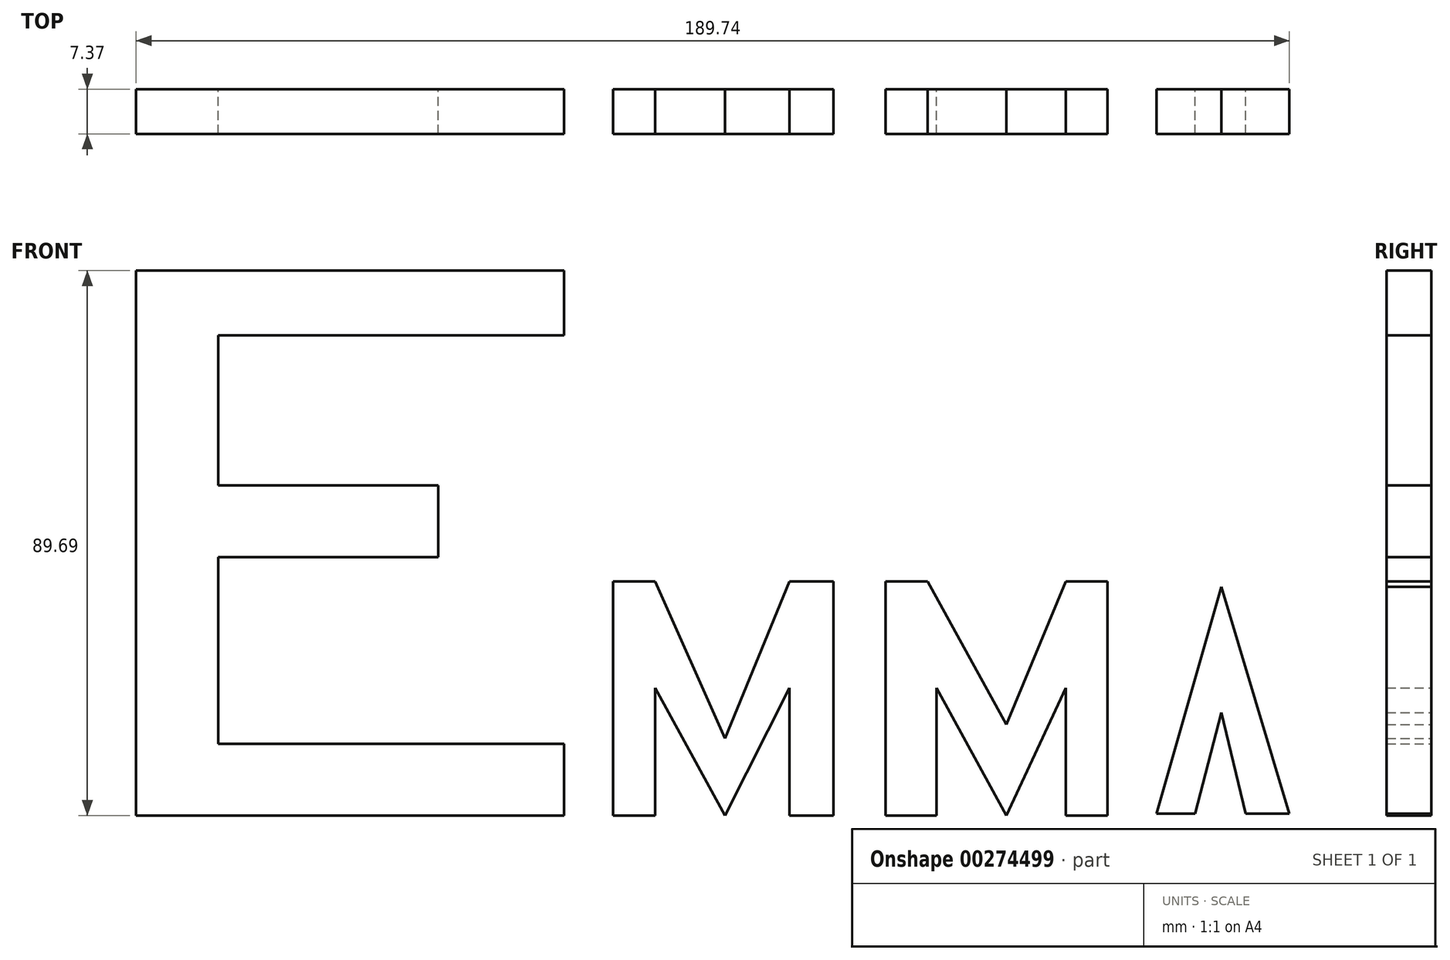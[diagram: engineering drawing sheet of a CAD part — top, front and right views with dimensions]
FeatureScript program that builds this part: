
annotation { "Feature Type Name" : "Feature", "Feature Type Description" : "" }
export const myFeature = defineFeature(function(context is Context, id is Id, definition is map)
    precondition{}
    {
        {
            var Q0;
            Q0=qCreatedBy(makeId("Front.planeOp"),FACE);
            var sketch = newSketch(context, id + "F0", { "sketchPlane" : qUnion([Q0])});
            skLineSegment(sketch, "E0", {"start": v(-135.03, 41.6) * mm, "end": v(-135.03, -48.1) * mm});
            skLineSegment(sketch, "E1", {"start": v(-135.03, -48.1) * mm, "end": v(-64.6, -48.1) * mm});
            skLineSegment(sketch, "E2", {"start": v(-64.6, -48.1) * mm, "end": v(-64.6, -36.32) * mm});
            skLineSegment(sketch, "E3", {"start": v(-64.6, -36.32) * mm, "end": v(-121.52, -36.32) * mm});
            skLineSegment(sketch, "E4", {"start": v(-121.52, -36.32) * mm, "end": v(-121.52, -5.56) * mm});
            skLineSegment(sketch, "E5", {"start": v(-121.52, -5.56) * mm, "end": v(-85.3, -5.56) * mm});
            skLineSegment(sketch, "E6", {"start": v(-85.3, -5.56) * mm, "end": v(-85.3, 6.23) * mm});
            skLineSegment(sketch, "E7", {"start": v(-85.3, 6.23) * mm, "end": v(-121.52, 6.23) * mm});
            skLineSegment(sketch, "E8", {"start": v(-121.52, 6.23) * mm, "end": v(-121.52, 30.95) * mm});
            skLineSegment(sketch, "E9", {"start": v(-121.52, 30.95) * mm, "end": v(-64.6, 30.95) * mm});
            skLineSegment(sketch, "E10", {"start": v(-64.6, 30.95) * mm, "end": v(-64.6, 41.6) * mm});
            skLineSegment(sketch, "E11", {"start": v(-64.6, 41.6) * mm, "end": v(-135.03, 41.6) * mm});
            skLineSegment(sketch, "E12", {"start": v(-56.55, -9.58) * mm, "end": v(-56.55, -48.1) * mm});
            skLineSegment(sketch, "E13", {"start": v(-56.55, -48.1) * mm, "end": v(-49.65, -48.1) * mm});
            skLineSegment(sketch, "E14", {"start": v(-49.65, -48.1) * mm, "end": v(-49.65, -27.12) * mm});
            skLineSegment(sketch, "E15", {"start": v(-49.65, -27.12) * mm, "end": v(-38.15, -48.1) * mm});
            skLineSegment(sketch, "E16", {"start": v(-38.15, -48.1) * mm, "end": v(-27.51, -27.12) * mm});
            skLineSegment(sketch, "E17", {"start": v(-27.51, -27.12) * mm, "end": v(-27.51, -48.1) * mm});
            skLineSegment(sketch, "E18", {"start": v(-27.51, -48.1) * mm, "end": v(-20.33, -48.1) * mm});
            skLineSegment(sketch, "E19", {"start": v(-20.33, -48.1) * mm, "end": v(-20.33, -9.58) * mm});
            skLineSegment(sketch, "E20", {"start": v(-20.33, -9.58) * mm, "end": v(-27.51, -9.58) * mm});
            skLineSegment(sketch, "E21", {"start": v(-27.51, -9.58) * mm, "end": v(-38.15, -35.45) * mm});
            skLineSegment(sketch, "E22", {"start": v(-38.15, -35.45) * mm, "end": v(-49.65, -9.58) * mm});
            skLineSegment(sketch, "E23", {"start": v(-49.65, -9.58) * mm, "end": v(-56.55, -9.58) * mm});
            skLineSegment(sketch, "E24", {"start": v(-11.7, -9.58) * mm, "end": v(-11.7, -48.1) * mm});
            skLineSegment(sketch, "E25", {"start": v(-11.7, -48.1) * mm, "end": v(-3.37, -48.1) * mm});
            skLineSegment(sketch, "E26", {"start": v(-3.37, -48.1) * mm, "end": v(-3.37, -27.12) * mm});
            skLineSegment(sketch, "E27", {"start": v(-3.37, -27.12) * mm, "end": v(8.13, -48.1) * mm});
            skLineSegment(sketch, "E28", {"start": v(8.13, -48.1) * mm, "end": v(17.9, -27.12) * mm});
            skLineSegment(sketch, "E29", {"start": v(17.9, -27.12) * mm, "end": v(17.9, -48.1) * mm});
            skLineSegment(sketch, "E30", {"start": v(17.9, -48.1) * mm, "end": v(24.8, -48.1) * mm});
            skLineSegment(sketch, "E31", {"start": v(24.8, -48.1) * mm, "end": v(24.8, -9.58) * mm});
            skLineSegment(sketch, "E32", {"start": v(24.8, -9.58) * mm, "end": v(17.9, -9.58) * mm});
            skLineSegment(sketch, "E33", {"start": v(17.9, -9.58) * mm, "end": v(8.13, -33.15) * mm});
            skLineSegment(sketch, "E34", {"start": v(8.13, -33.15) * mm, "end": v(-4.78, -9.58) * mm});
            skLineSegment(sketch, "E35", {"start": v(-4.78, -9.58) * mm, "end": v(-11.7, -9.58) * mm});
            skLineSegment(sketch, "E36", {"start": v(32.86, -47.82) * mm, "end": v(39.18, -47.82) * mm});
            skLineSegment(sketch, "E37", {"start": v(39.18, -47.82) * mm, "end": v(43.5, -31.14) * mm});
            skLineSegment(sketch, "E38", {"start": v(43.5, -31.14) * mm, "end": v(47.52, -47.82) * mm});
            skLineSegment(sketch, "E39", {"start": v(47.52, -47.82) * mm, "end": v(54.7, -47.82) * mm});
            skLineSegment(sketch, "E40", {"start": v(54.7, -47.82) * mm, "end": v(43.5, -10.44) * mm});
            skLineSegment(sketch, "E41", {"start": v(43.5, -10.44) * mm, "end": v(32.86, -47.82) * mm});
            skSolve(sketch);
        }
        {
            var Q0;
            Q0 = qSketchRegion(id + "F0", true);
            extrude(context, id + "F1", {"entities" : qUnion([Q0]), "depth" : 7.37 * mm});
        }
    });
